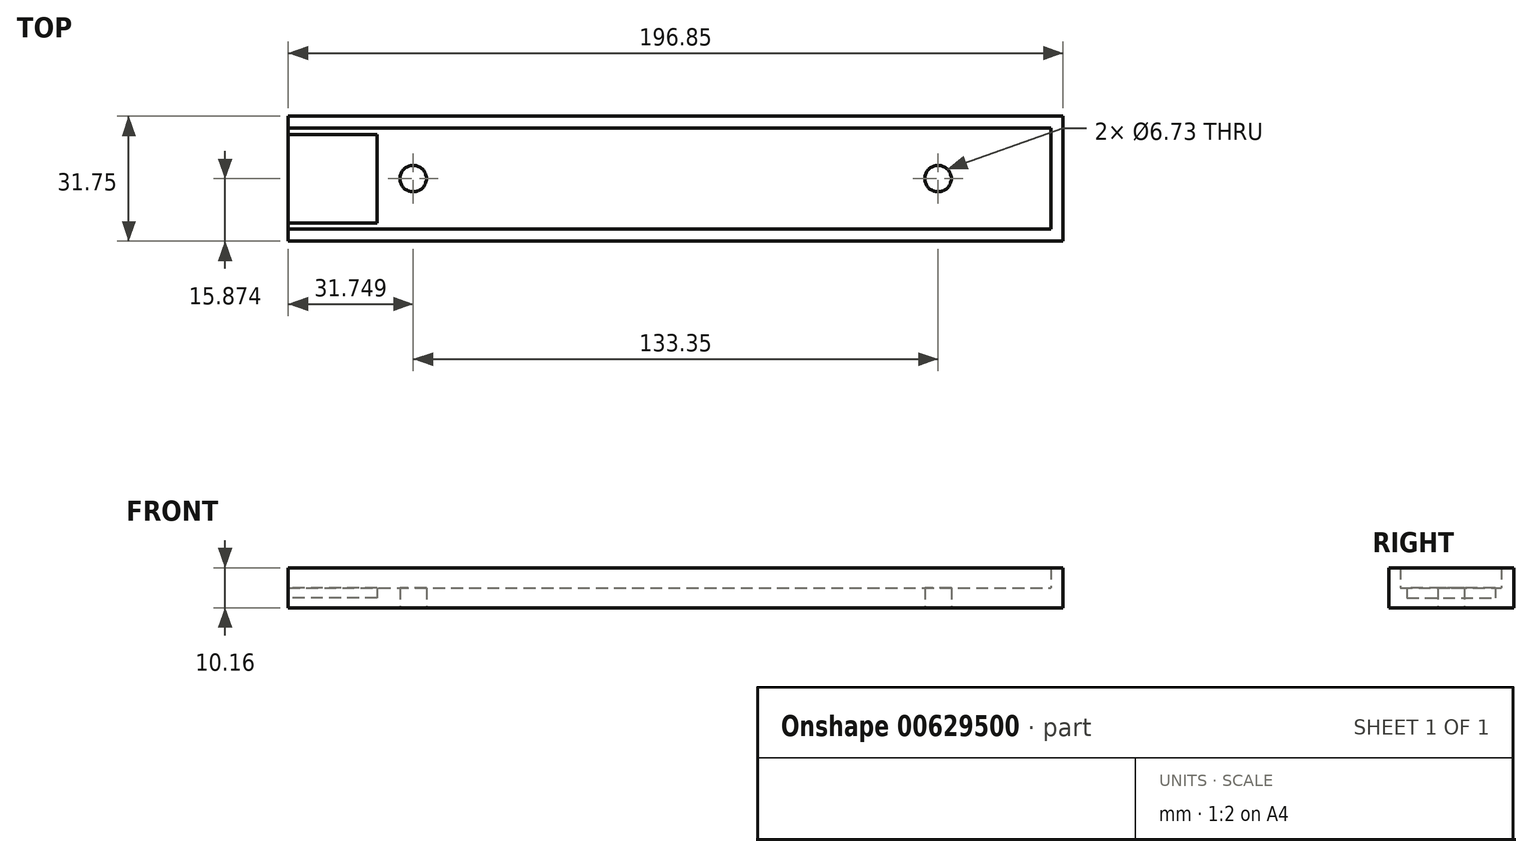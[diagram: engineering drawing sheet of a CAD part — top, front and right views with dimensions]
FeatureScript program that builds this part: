
annotation { "Feature Type Name" : "Feature", "Feature Type Description" : "" }
export const myFeature = defineFeature(function(context is Context, id is Id, definition is map)
    precondition{}
    {
        {
            var Q0;
            Q0=qCreatedBy(makeId("Top.planeOp"),FACE);
            var sketch = newSketch(context, id + "F0", { "sketchPlane" : qUnion([Q0])});
            skLineSegment(sketch, "E0.bottom", {"start": v(-44.03, -14.21) * mm, "end": v(152.82, -14.21) * mm});
            skLineSegment(sketch, "E0.top", {"start": v(-44.03, 17.54) * mm, "end": v(152.82, 17.54) * mm});
            skLineSegment(sketch, "E0.left", {"start": v(-44.03, -14.21) * mm, "end": v(-44.03, 17.54) * mm});
            skLineSegment(sketch, "E0.right", {"start": v(152.82, -14.21) * mm, "end": v(152.82, 17.54) * mm});
            skCircle(sketch, "E1", {"center": v(-12.28, 1.66) * mm, "radius": 3.37 * mm});
            skCircle(sketch, "E2", {"center": v(121.07, 1.66) * mm, "radius": 3.37 * mm});
            skLineSegment(sketch, "E3.0", {"start": v(-44.03, 14.5) * mm, "end": v(149.77, 14.5) * mm});
            skLineSegment(sketch, "E3.2", {"start": v(-44.03, -11.16) * mm, "end": v(149.77, -11.16) * mm});
            skLineSegment(sketch, "E3.3", {"start": v(149.77, -11.16) * mm, "end": v(149.77, 14.5) * mm});
            skPoint(sketch, "E4.endSnap0", {"position": v(-44.03, 1.66) * mm});
            skLineSegment(sketch, "E5.0", {"start": v(-21.45, 12.9) * mm, "end": v(-44.03, 12.9) * mm});
            skLineSegment(sketch, "E6.0", {"start": v(-21.45, -9.56) * mm, "end": v(-44.03, -9.56) * mm});
            skLineSegment(sketch, "E7.trimOffspring", {"start": v(-21.45, 12.9) * mm, "end": v(-21.45, -9.56) * mm});
            skSolve(sketch);
        }
        {
            var Q0;
            {var subQ1=sQuery(id+"F0.wireOp",EDGE,"E0.bottom");Q0=makeQuery(id+"F0.imprint","IMPRINT",FACE,{"disambiguationData":[TD([[makeQuery(id+"F0.imprint","IMPRINT",EDGE,{"derivedFrom":subQ1}),1.0]])]});}
            extrude(context, id + "F1", {"entities" : qUnion([Q0]), "depth" : 10.16 * mm, "offsetDistance" : 25.4 * mm});
        }
        {
            var Q0;
            Q0=makeQuery(id+"F0.imprint","IMPRINT",FACE,{"disambiguationData":[TD([[makeQuery(id+"F0.imprint","IMPRINT",EDGE,{"derivedFrom":sQuery(id+"F0.wireOp",EDGE,"E1")}),-1.0]])]});
            var Q1;
            {var subQ0=sQuery(id+"F0.wireOp",EDGE,"E5.0");Q1=makeQuery(id+"F0.imprint","IMPRINT",FACE,{"disambiguationData":[TD([[makeQuery(id+"F0.imprint","IMPRINT",EDGE,{"derivedFrom":subQ0}),1.0]])]});}
            extrude(context, id + "F2", {"entities" : qUnion([Q0, Q1]), "operationType" : NewBodyOperationType.ADD, "depth" : 5.08 * mm, "offsetDistance" : 25.4 * mm});
        }
        {
            var Q0;
            {var subQ0=sQuery(id+"F0.wireOp",EDGE,"E5.0");Q0=makeQuery(id+"F0.imprint","IMPRINT",FACE,{"disambiguationData":[TD([[makeQuery(id+"F0.imprint","IMPRINT",EDGE,{"derivedFrom":subQ0}),1.0]])]});}
            extrude(context, id + "F3", {"entities" : qUnion([Q0]), "operationType" : NewBodyOperationType.REMOVE, "depth" : 5.08 * mm, "offsetDistance" : 25.4 * mm, "hasSecondDirection" : true, "secondDirectionOppositeDirection" : false, "secondDirectionDepth" : 2.54 * mm});
        }
    });
